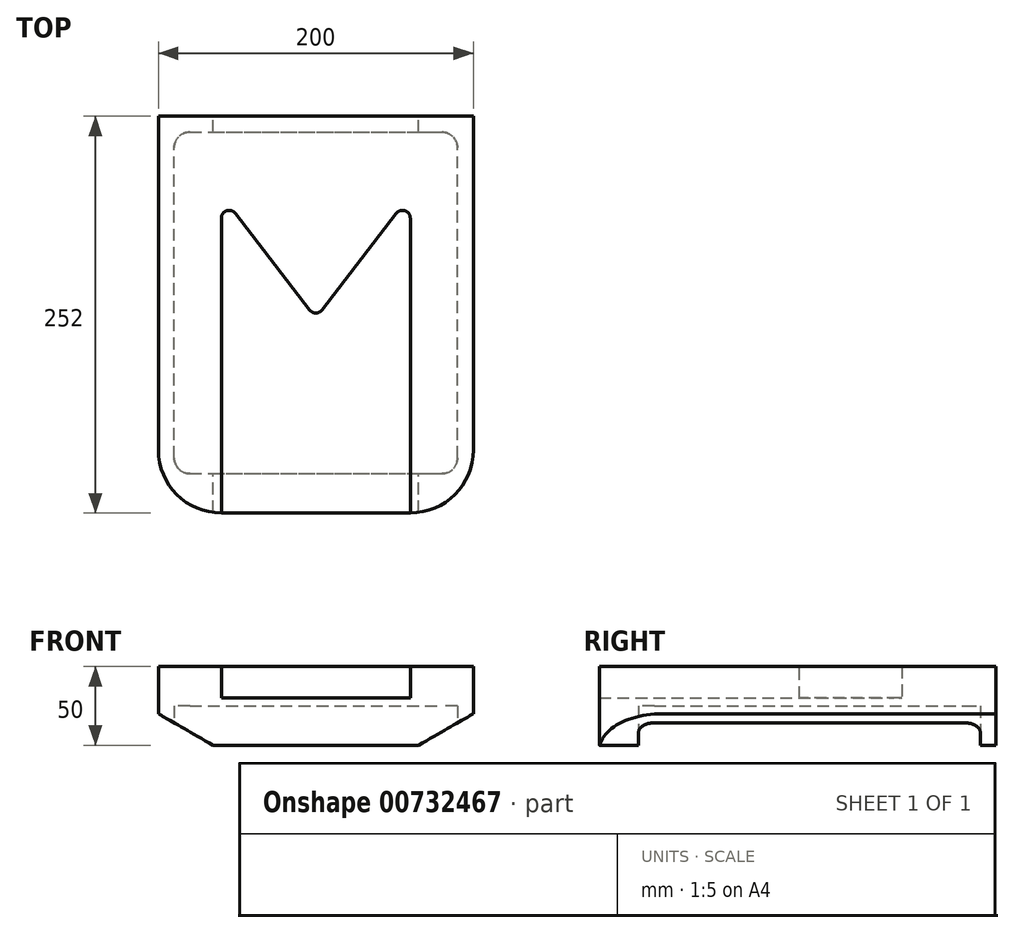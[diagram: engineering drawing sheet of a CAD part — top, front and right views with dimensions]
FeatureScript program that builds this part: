
annotation { "Feature Type Name" : "Feature", "Feature Type Description" : "" }
export const myFeature = defineFeature(function(context is Context, id is Id, definition is map)
    precondition{}
    {
        {
            var Q0;
            Q0=qCreatedBy(makeId("Front.planeOp"),FACE);
            var sketch = newSketch(context, id + "F0", { "sketchPlane" : qUnion([Q0])});
            skLineSegment(sketch, "E0", {"start": v(0, 0) * mm, "end": v(100, 0) * mm});
            skLineSegment(sketch, "E1", {"start": v(100, 0) * mm, "end": v(100, -30) * mm});
            skLineSegment(sketch, "E2", {"start": v(100, -30) * mm, "end": v(65.36, -50) * mm});
            skLineSegment(sketch, "E3", {"start": v(65.36, -50) * mm, "end": v(0, -50) * mm});
            skLineSegment(sketch, "E4", {"start": v(0, -50) * mm, "end": v(0, 0) * mm});
            skSolve(sketch);
        }
        {
            var Q0;
            Q0 = qSketchRegion(id + "F0", true);
            extrude(context, id + "F1", {"entities" : qUnion([Q0]), "depth" : 252 * mm, "offsetDistance" : 25.4 * mm});
        }
        {
            var Q0;
            Q0=makeQuery(id+"F1.opExtrude","SWEPT_BODY",BODY,{"disambiguationData":[OSD([sQuery(id+"F0.wireOp",EDGE,"E0"),sQuery(id+"F0.wireOp",EDGE,"E1"),sQuery(id+"F0.wireOp",EDGE,"E2"),sQuery(id+"F0.wireOp",EDGE,"E3"),sQuery(id+"F0.wireOp",EDGE,"E4")])]});
            var Q1;
            Q1=qCreatedBy(makeId("Right.planeOp"),FACE);
            mirror(context, id + "F2", {"operationType" : NewBodyOperationType.ADD, "entities" : qUnion([Q0]), "mirrorPlane" : qUnion([Q1])});
        }
        {
            var Q0;
            {var subQ0=makeQuery(id+"F1.opExtrude","SWEPT_FACE",FACE,{"disambiguationData":[OSD([sQuery(id+"F0.wireOp",EDGE,"E0")])]});Q0=makeQuery(id+"F2.boolean.opBoolean","MERGE",FACE,{"derivedFrom":[subQ0,makeQuery(id+"F2.opPattern","COPY",FACE,{"derivedFrom":subQ0,"instanceName":"1"})]});}
            var sketch = newSketch(context, id + "F3", { "sketchPlane" : qUnion([Q0])});
            skLineSegment(sketch, "E5", {"start": v(60, -252) * mm, "end": v(60, -50) * mm});
            skLineSegment(sketch, "E6", {"start": v(60, -50) * mm, "end": v(0, -128.2) * mm});
            skLineSegment(sketch, "E7", {"start": v(0, -128.2) * mm, "end": v(-60, -50) * mm});
            skLineSegment(sketch, "E8", {"start": v(-60, -50) * mm, "end": v(-60, -252) * mm});
            skLineSegment(sketch, "E9", {"start": v(-60, -252) * mm, "end": v(60, -252) * mm});
            skSolve(sketch);
        }
        {
            var Q0;
            Q0=makeQuery(id+"F3.imprint","IMPRINT",FACE,{"disambiguationData":[TD([[makeQuery(id+"F3.imprint","IMPRINT",EDGE,{"derivedFrom":sQuery(id+"F3.wireOp",EDGE,"E5")}),1.0]])]});
            extrude(context, id + "F4", {"entities" : qUnion([Q0]), "operationType" : NewBodyOperationType.REMOVE, "oppositeDirection" : true, "depth" : 20 * mm, "offsetDistance" : 25 * mm});
        }
        {
            var Q0;
            {var subQ0=makeQuery(id+"F1.opExtrude","SWEPT_FACE",FACE,{"disambiguationData":[OSD([sQuery(id+"F0.wireOp",EDGE,"E0")])]});Q0=makeQuery(id+"F2.boolean.opBoolean","MERGE",FACE,{"derivedFrom":[subQ0,makeQuery(id+"F2.opPattern","COPY",FACE,{"derivedFrom":subQ0,"instanceName":"1"})]});}
            var sketch = newSketch(context, id + "F5", { "sketchPlane" : qUnion([Q0])});
            skArc(sketch, "E10", {"start": v(60, -252) * mm, "mid": v(88.28, -240.28) * mm, "end": v(100, -212) * mm});
            skArc(sketch, "E11", {"start": v(-100, -212) * mm, "mid": v(-88.28, -240.28) * mm, "end": v(-60, -252) * mm});
            skLineSegment(sketch, "E12", {"start": v(60, -252) * mm, "end": v(-60, -252) * mm});
            skLineSegment(sketch, "E13", {"start": v(-100, -212) * mm, "end": v(-100, 0) * mm});
            skLineSegment(sketch, "E14", {"start": v(-100, 0) * mm, "end": v(100, 0) * mm});
            skLineSegment(sketch, "E15", {"start": v(100, 0) * mm, "end": v(100, -212) * mm});
            skSolve(sketch);
        }
        {
            var Q0;
            {var subQ0=sQuery(id+"F5.wireOp",EDGE,"E10");Q0=makeQuery(id+"F5.imprint","IMPRINT",FACE,{"disambiguationData":[TD([[makeQuery(id+"F5.imprint","IMPRINT",EDGE,{"derivedFrom":subQ0}),-1.0]])]});}
            var Q1;
            {var subQ0=sQuery(id+"F5.wireOp",EDGE,"E11");Q1=makeQuery(id+"F5.imprint","IMPRINT",FACE,{"disambiguationData":[TD([[makeQuery(id+"F5.imprint","IMPRINT",EDGE,{"derivedFrom":subQ0}),-1.0]])]});}
            extrude(context, id + "F6", {"entities" : qUnion([Q0, Q1]), "operationType" : NewBodyOperationType.REMOVE, "endBound" : BoundingType.THROUGH_ALL, "oppositeDirection" : true, "depth" : 25 * mm, "offsetDistance" : 25 * mm});
        }
        {
            var Q0;
            Q0=makeQuery(id+"F4.boolean.opBoolean","COPY",EDGE,{"derivedFrom":makeQuery(id+"F4.opExtrude","SWEPT_EDGE",EDGE,{"disambiguationData":[OSD([sQuery(id+"F3.wireOp",EDGE,"E6"),sQuery(id+"F3.wireOp",EDGE,"E7")])]})});
            fillet(context, id + "F7", {"entities" : qUnion([Q0]), "radius" : 5 * mm, "tangentPropagation" : true, "allowEdgeOverflow" : false});
        }
        {
            var Q0;
            Q0=makeQuery(id+"F4.boolean.opBoolean","COPY",EDGE,{"derivedFrom":makeQuery(id+"F4.opExtrude","SWEPT_EDGE",EDGE,{"disambiguationData":[OSD([sQuery(id+"F3.wireOp",EDGE,"E5"),sQuery(id+"F3.wireOp",EDGE,"E6")])]})});
            var Q1;
            Q1=makeQuery(id+"F4.boolean.opBoolean","COPY",EDGE,{"derivedFrom":makeQuery(id+"F4.opExtrude","SWEPT_EDGE",EDGE,{"disambiguationData":[OSD([sQuery(id+"F3.wireOp",EDGE,"E7"),sQuery(id+"F3.wireOp",EDGE,"E8")])]})});
            fillet(context, id + "F8", {"entities" : qUnion([Q0, Q1]), "radius" : 5 * mm, "tangentPropagation" : true, "allowEdgeOverflow" : false});
        }
        {
            var Q0;
            {var subQ0=makeQuery(id+"F1.opExtrude","SWEPT_FACE",FACE,{"disambiguationData":[OSD([sQuery(id+"F0.wireOp",EDGE,"E3")])]});Q0=makeQuery(id+"F2.boolean.opBoolean","MERGE",FACE,{"derivedFrom":[subQ0,makeQuery(id+"F2.opPattern","COPY",FACE,{"derivedFrom":subQ0,"instanceName":"1"})]});}
            var sketch = newSketch(context, id + "F9", { "sketchPlane" : qUnion([Q0])});
            skLineSegment(sketch, "E16.bottom", {"start": v(-90, 227) * mm, "end": v(90, 227) * mm});
            skLineSegment(sketch, "E16.top", {"start": v(-90, 10) * mm, "end": v(90, 10) * mm});
            skLineSegment(sketch, "E16.left", {"start": v(-90, 227) * mm, "end": v(-90, 10) * mm});
            skLineSegment(sketch, "E16.right", {"start": v(90, 227) * mm, "end": v(90, 10) * mm});
            skPoint(sketch, "E16.middle", {"position": v(0, 118.5) * mm});
            skSolve(sketch);
        }
        {
            var Q0;
            Q0 = qSketchRegion(id + "F9", true);
            extrude(context, id + "F10", {"entities" : qUnion([Q0]), "operationType" : NewBodyOperationType.REMOVE, "oppositeDirection" : true, "depth" : 25 * mm, "offsetDistance" : 25 * mm});
        }
        {
            var Q0;
            Q0=makeQuery(id+"F10.boolean.opBoolean","COPY",EDGE,{"derivedFrom":makeQuery(id+"F10.opExtrude","SWEPT_EDGE",EDGE,{"disambiguationData":[OSD([sQuery(id+"F9.wireOp",EDGE,"E16.top"),sQuery(id+"F9.wireOp",EDGE,"E16.right")])]})});
            var Q1;
            Q1=makeQuery(id+"F10.boolean.opBoolean","COPY",EDGE,{"derivedFrom":makeQuery(id+"F10.opExtrude","SWEPT_EDGE",EDGE,{"disambiguationData":[OSD([sQuery(id+"F9.wireOp",EDGE,"E16.top"),sQuery(id+"F9.wireOp",EDGE,"E16.left")])]})});
            var Q2;
            Q2=makeQuery(id+"F10.boolean.opBoolean","COPY",EDGE,{"derivedFrom":makeQuery(id+"F10.opExtrude","SWEPT_EDGE",EDGE,{"disambiguationData":[OSD([sQuery(id+"F9.wireOp",EDGE,"E16.bottom"),sQuery(id+"F9.wireOp",EDGE,"E16.left")])]})});
            var Q3;
            Q3=makeQuery(id+"F10.boolean.opBoolean","COPY",EDGE,{"derivedFrom":makeQuery(id+"F10.opExtrude","SWEPT_EDGE",EDGE,{"disambiguationData":[OSD([sQuery(id+"F9.wireOp",EDGE,"E16.bottom"),sQuery(id+"F9.wireOp",EDGE,"E16.right")])]})});
            fillet(context, id + "F11", {"entities" : qUnion([Q0, Q1, Q2, Q3]), "radius" : 10 * mm, "tangentPropagation" : true, "allowEdgeOverflow" : false});
        }
    });
